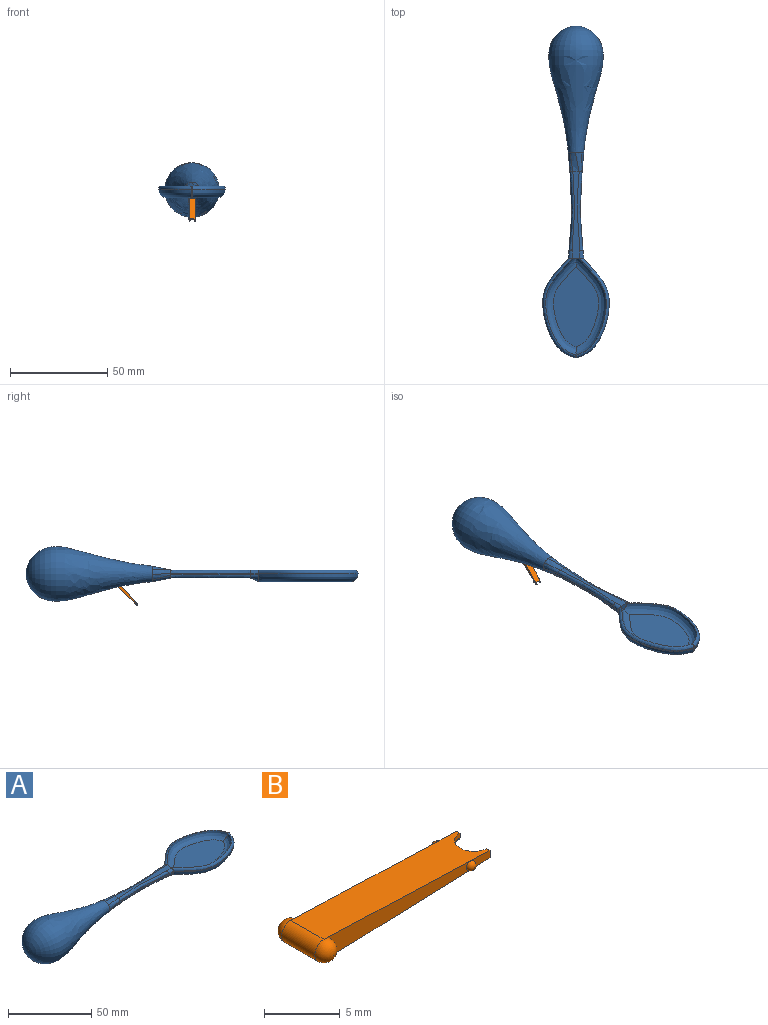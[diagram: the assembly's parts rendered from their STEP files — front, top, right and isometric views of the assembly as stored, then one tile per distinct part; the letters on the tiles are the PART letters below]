
ASSEMBLY  parts=2 mates=1
PART A: 68 faces, bbox 172.6x35.9x29.8 mm
  f0: plane 17.5x3.7mm, normal (0,-1,0), area 36.5mm2, adj f45,f46,f47,f48,f51,f52,f53,f54
  f1: plane 17.58x3.68mm, normal (0,1,0), area 36.5mm2, adj f45,f46,f47,f48,f49,f50,f53,f54
  f2: bspline ~60.54x3.63mm, area 99.3mm2, adj f8,f9,f12,f44
  f3: bspline ~60.54x3.63mm, area 99.3mm2, adj f7,f9,f10,f39
  f4: bspline ~60.54x3.63mm, area 99.3mm2, adj f6,f8,f14,f42
  f5: bspline ~60.54x3.63mm, area 99.3mm2, adj f6,f7,f16,f41
  f6: plane 46.79x6.2mm, normal (0,0,1), area 106mm2, adj f4,f5,f15,f31,f32,f33,f41,f42
  f7: extruded ~41.18x1.46mm, area 41.3mm2, adj f3,f5,f17,f40
  f8: extruded ~41.18x1.46mm, area 41.3mm2, adj f2,f4,f13,f43
  f9: plane 42.44x6.2mm, normal (0,0,-1), area 87.2mm2, adj f2,f3,f11,f38
  f10: bspline ~9.87x3.57mm, area 27mm2, adj f3,f11,f17,f45
  f11: bspline ~10x4.73mm, area 31.5mm2, adj f9,f10,f12,f45
  f12: bspline ~9.87x2.94mm, area 26.1mm2, adj f2,f11,f13,f45
  f13: bspline ~9.49x3.61mm, area 19.4mm2, adj f8,f12,f14,f45
  f14: bspline ~9.87x3.57mm, area 27mm2, adj f4,f13,f15,f45
  f15: bspline ~10x4.73mm, area 31.5mm2, adj f6,f14,f16,f45
  f16: bspline ~9.87x2.94mm, area 26.1mm2, adj f5,f15,f17,f45
  f17: bspline ~9.49x3.61mm, area 19.4mm2, adj f7,f10,f16,f45
  f18: extruded ~51.02x16.77mm, area 31.1mm2, adj f21,f24,f30,f34
  f19: extruded ~51.02x16.77mm, area 31.1mm2, adj f20,f23,f30,f37
  f20: bspline ~53.29x17.63mm, area 145.5mm2, adj f19,f27,f28,f32
  f21: bspline ~53.29x17.63mm, area 145.5mm2, adj f18,f26,f28,f33
  f22: plane 45.36x26.21mm, normal (0,0,-1), area 826mm2, adj f23,f24
  f23: bspline ~54.51x19.15mm, area 379.1mm2, adj f19,f22,f24,f29,f36
  f24: bspline ~54.51x19.15mm, area 379.1mm2, adj f18,f22,f23,f29,f35
  f25: plane 41.53x23.21mm, normal (0,0,1), area 669.1mm2, adj f26,f27
  f26: bspline ~56.82x22.93mm, area 359.7mm2, adj f21,f25,f27,f31
  f27: bspline ~56.82x22.93mm, area 359.7mm2, adj f20,f25,f26,f31
  f28: bspline ~1.69x1.59mm, area 0.7mm2, adj f20,f21,f30
  f29: bspline ~4.32x4.25mm, area 1.8mm2, adj f23,f24,f30
  f30: cylinder r=1mm len=0.67mm, axis (0,0,-1), area 0.3mm2, adj f18,f19,f28,f29
  f31: plane 4.58x3.73mm, normal (1,0,0), area 8.4mm2, adj f6,f26,f27
  f32: extruded ~2.04x1.5mm, area 0.7mm2, adj f6,f20,f37,f41
  f33: extruded ~2.04x1.5mm, area 0.7mm2, adj f6,f21,f34,f42
  f34: plane 0.5x0.25mm, normal (0,1,0), area 0.1mm2, adj f18,f33,f35,f43
  f35: extruded ~4x3.86mm, area 1.5mm2, adj f24,f34,f36,f44
  f36: extruded ~4x3.86mm, area 1.5mm2, adj f23,f35,f37,f38,f39
  f37: plane 0.5x0.25mm, normal (0,-1,0), area 0.1mm2, adj f19,f32,f36,f40
  f38: bspline ~4.75x4.51mm, area 16.6mm2, adj f9,f36,f39,f44
  f39: bspline ~4.3x2.61mm, area 10.8mm2, adj f3,f36,f38,f40
  f40: bspline ~3.84x1mm, area 2.9mm2, adj f7,f37,f39,f41
  f41: bspline ~4.3x2.04mm, area 10.6mm2, adj f5,f6,f32,f40
  f42: bspline ~4.3x2.04mm, area 10.6mm2, adj f4,f6,f33,f43
  f43: bspline ~3.84x1mm, area 2.9mm2, adj f8,f34,f42,f44
  f44: bspline ~4.3x4mm, area 17.6mm2, adj f2,f35,f38,f43
  f45: revolved ~65x28.09mm, area 4074.6mm2, adj f0,f1,f10,f11,f12,f13,f14,f15
  f46: plane 3.24x1.27mm, normal (-1,0,0), area 3.8mm2, adj f0,f1,f45,f48
  f47: plane 3.24x2.63mm, normal (1,0,0), area 8.5mm2, adj f0,f1,f48,f53
  f48: plane 17.5x3.24mm, normal (0,0,-1), area 56.7mm2, adj f0,f1,f46,f47
  f49: sphere r=0.88mm, area 4.8mm2, adj f1
  f50: sphere r=0.38mm, area 0.9mm2, adj f1
  f51: sphere r=0.88mm, area 4.8mm2, adj f0
  f52: sphere r=0.38mm, area 0.9mm2, adj f0
  f53: plane 3.24x1mm, normal (0,0,1), area 3.2mm2, adj f0,f1,f47,f54
  f54: plane 3.24x1.44mm, normal (0.56,0,0.83), area 5.6mm2, adj f0,f1,f53,f55
  f55: extruded ~3.24x3.21mm, area 9.8mm2, adj f45,f54,f56
  f56: torus R=6.55mm, axis (-1,0,0), area 1mm2, adj f45,f55
  f57: revolved ~13.72x13.72mm, area 290.7mm2, adj f58,f59
  f58: plane 10.25x10.25mm, normal (-1,0,0), area 82.4mm2, adj f57
  f59: plane 13.72x13.72mm, normal (1,0,0), area 147.9mm2, adj f57
  f60: plane 17.45x17.45mm, normal (1,0,0), area 239.1mm2, adj f61
  f61: revolved ~17.45x17.45mm, area 389.4mm2, adj f60,f62
  f62: plane 14.97x14.97mm, normal (-1,0,0), area 176mm2, adj f61
  f63: plane 16.29x16.29mm, normal (1,0,0), area 208.3mm2, adj f64
  f64: revolved ~18.17x18.17mm, area 425.2mm2, adj f63,f65
  f65: plane 18.02x18.02mm, normal (-1,0,0), area 255.1mm2, adj f64
  f66: revolved ~11.76x11.75mm, area 127.2mm2, adj f67
  f67: plane 11.77x11.77mm, normal (-1,0,0), area 108.8mm2, adj f66
PART B: 15 faces, bbox 16.4x4.9x1.8 mm
  f0: plane 1.81x0.73mm, normal (0,1,0), area 1mm2, adj f2,f5,f7,f13
  f1: plane 1.81x0.73mm, normal (0,-1,0), area 1mm2, adj f4,f5,f7,f12
  f2: plane 0.6x0.3mm, normal (1,0,0), area 0.2mm2, adj f0,f5,f7,f9,f14
  f3: plane 13.63x1.7mm, normal (0,1,0), area 15.3mm2, adj f5,f7,f10,f13
  f4: plane 0.6x0.3mm, normal (1,0,0), area 0.2mm2, adj f1,f5,f7,f9,f14
  f5: plane 15.5x3.1mm, normal (0.04,0,-1), area 44.6mm2, adj f0,f1,f2,f3,f4,f6,f8,f10
  f6: cylinder r=0.85mm len=3.1mm, axis (0,-1,0), area 8.3mm2, adj f5,f7,f10,f11
  f7: plane 15.59x3.19mm, normal (0.04,0,1), area 45.6mm2, adj f0,f1,f2,f3,f4,f6,f8,f9
  f8: plane 13.63x1.7mm, normal (0,-1,0), area 15.3mm2, adj f5,f7,f11,f12
  f9: cylinder r=1.25mm len=2.5mm, axis (0,0,-1), area 1.4mm2, adj f2,f4,f7,f14
  f10: sphere r=0.85mm, area 4.5mm2, adj f3,f5,f6,f7
  f11: sphere r=0.85mm, area 4.5mm2, adj f5,f6,f7,f8
  f12: sphere r=0.36mm, area 0.8mm2, adj f1,f8
  f13: sphere r=0.36mm, area 0.8mm2, adj f0,f3
  f14: bspline ~3x1.5mm, area 1.6mm2, adj f2,f4,f5,f9
PLACE A rot(axis=(0,0,-1),90deg) t=(0,25.12,0)mm
PLACE B rot(axis=(0.36,0.36,-0.86),98.8deg) t=(-1.48,-56.09,-14.61)mm
MATE revolute B.f6 <-> A.f0  axis (1,0,0) through (1.62,-46.62,-4.75)mm
